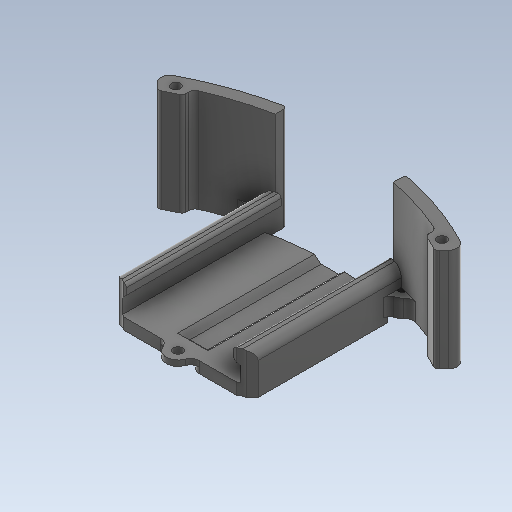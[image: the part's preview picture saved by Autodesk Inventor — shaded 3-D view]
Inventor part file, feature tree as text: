
AUTODESK INVENTOR PART (.ipt)
format: ipt  version: 2020 (Build 240168000, 168)  size: 1,015,296 bytes
history: native  units: mm
features: projected_geometry x25, other x11, sketch x11, extrude x10, fillet x3, chamfer x1
ambient origin geometry x8: Origin, YZ Plane, XZ Plane, XY Plane, X Axis, Y Axis, Z Axis, Center Point
bodies: Body1 (feature_tree)
feature tree (61):
  other  "Твердое тело1"
  sketch  "Эскиз1"
  other  "РабПлоскость4"
  sketch  "Эскиз2"
  other  "РабПлоскость5"
  sketch  "Эскиз3"
  other  "РабПлоскость6"
  sketch  "Эскиз4"
  other  "РабПлоскость7"
  sketch  "Эскиз5"
  other  "РабПлоскость8"
  sketch  "Эскиз6"
  extrude  "Выдавливание9"  TaperAngle=45.0deg  [1 undecoded]
  extrude  "Выдавливание10"  Depth=7.0mm
  other  "РабПлоскость1"
  extrude  "Выдавливание11"  Depth=20.0mm
  chamfer  "Фаска1"  Distance=7.0mm
  fillet  "Сопряжение1"  Radius=3.2mm
  fillet  "Сопряжение2"  Radius=59.0mm
  other  "РабПлоскость2"
  extrude  "Выдавливание12"  Depth=83.0mm
  other  "РабПлоскость9"
  sketch  "Эскиз9"
  extrude  "Выдавливание13"  Depth=69.0mm
  extrude  "Выдавливание14"  Depth=55.0mm
  other  "РабПлоскость3"
  extrude  "Выдавливание15"  Depth=3.0mm
  extrude  "Выдавливание16"  Depth=8.0mm
  extrude  "Выдавливание17"  Depth=5.0mm
  other  "РабПлоскость10"
  extrude  "Выдавливание18"  Depth=2.0mm
  fillet  "Сопряжение4"  Radius=40.0mm
  projected_geometry  "Спроецированная петля1"
  projected_geometry  "Спроецированная петля2"
  projected_geometry  "Спроецированная петля3"
  projected_geometry  "Спроецированная петля4"
  projected_geometry  "Спроецированная петля5"
  sketch  "Эскиз7"
  projected_geometry  "Спроецированная петля6"
  projected_geometry  "Спроецированная петля7"
  projected_geometry  "Спроецированная петля8"
  sketch  "Эскиз8"
  projected_geometry  "Спроецированная петля13"
  projected_geometry  "Спроецированная петля14"
  projected_geometry  "Спроецированная петля15"
  sketch  "Эскиз10"
  projected_geometry  "Спроецированная петля16"
  projected_geometry  "Спроецированная петля18"
  projected_geometry  "Спроецированная петля19"
  projected_geometry  "Спроецированная петля21"
  projected_geometry  "Спроецированная петля24"
  projected_geometry  "Спроецированная петля25"
  sketch  "Эскиз12"
  projected_geometry  "Спроецированная петля26"
  projected_geometry  "Спроецированная петля27"
  projected_geometry  "Спроецированная петля28"
  projected_geometry  "Спроецированная петля29"
  projected_geometry  "Спроецированная петля30"
  projected_geometry  "Спроецированная петля31"
  projected_geometry  "Спроецированная петля32"
  projected_geometry  "Спроецированная петля33"
note: 1 required parameter value undecoded (feature->parameter linkage not recoverable at this tier; creation-order binding heuristic only, values carry confidence <= 0.55)
